# Revit family: Скамейка «Архимед»
name_source: partatom
category: Антураж
revit_build: Autodesk Revit 2017 (Build: 20160225_1515(x64)
units: mm (PartAtom-declared; Revit-internal decimal feet)

## family parameters
Всегда вертикально = Да
Источник визуального образа = Геометрия семейства
На основе рабочей плоскости = Нет
Общий = Нет
При загрузке вырезать с полостями = Нет
Точка расчета площади = Нет

## types (8) — shared parameters
ADSK_Код изделия = 11478
ADSK_Материал доски = Сосна, лучистая
ADSK_Материал опоры = Сталь, окрашенная, темно-серая, матовая
ADSK_Материал фурнитуры = Сталь, окрашенная, темно-серая, матовая
ADSK_Наименование = Скамейка «Архимед»
ADSK_Размер_Высота = 926 мм
ADSK_Размер_Ширина = 921 мм
URL = https://hobbyka.ru
Изготовитель = ООО "Хоббика"
zero-valued in all types: Высота

## per-type parameters (varying)
| type | ADSK_Размер_Длина | Стоимость | Центральная опора |
| Скамейка «Архимед» 1,2м | 1200 мм | 26532 $ | Нет |
| Скамейка «Архимед» 1,5м | 1500 мм | 28023 $ | Нет |
| Скамейка «Архимед» 1,8м | 1800 мм | 30310 $ | Нет |
| Скамейка «Архимед» 2,0м | 2000 мм | 31835 $ | Нет |
| Скамейка «Архимед» 2,0м (3опоры) | 3000 мм | 26532 $ | Да |
| Скамейка «Архимед» 2,5м (3 опоры) | 2500 мм | 43287 $ | Да |
| Скамейка «Архимед» 3,0м (3 опоры) | 2500 мм | 47099 $ | Да |
| Скамейка «Архимед» 5,5м | 5500 мм | 76767 $ | Да |
